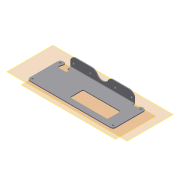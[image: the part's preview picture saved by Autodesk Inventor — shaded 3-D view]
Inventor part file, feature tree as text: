
AUTODESK INVENTOR PART (.ipt)
format: ipt  version: 2014 (Build 180170000, 170)  size: 222,720 bytes
history: native  units: mm
features: fillet x6, sketch x5, sheet_metal_op x4, reference x4, extrude x3, plane x2, other x2
ambient origin geometry x8: Origin, YZ Plane, XZ Plane, XY Plane, X Axis, Y Axis, Z Axis, Center Point
bodies: Solid1 (feature_tree)
feature tree (26):
  plane  "Work Plane1"
  sheet_metal_op  "Face1"
  fillet  "Fillet1"  Radius=1.0mm
  plane  "Work Plane2"
  extrude  "Extrusion4"  Depth=1.0mm
  sheet_metal_op  "Flange3"
  fillet  "Fillet2"  Radius=1.0mm
  fillet  "Fillet3"  Radius=5.0mm
  extrude  "Extrusion5"  Depth=5.0mm
  fillet  "Fillet4"  Radius=7.0mm
  fillet  "Fillet5"  Radius=1.5mm
  extrude  "Extrusion6"  Depth=5.0mm
  fillet  "Fillet6"  Radius=10.0mm
  sketch  "Sketch1"  dims[d1=1.0mm d2=1.0mm d3=1.0mm d4=5.0mm]
  reference  "Reference1"
  reference  "Reference2"
  reference  "Reference3"
  reference  "Reference4"
  other  "Plate1"
  sketch  "Sketch7"  dims[d5=7.0mm d6=5.0mm d7=7.0mm d8=1.5mm]
  sketch  "Sketch8"  dims[d48=1.0mm d49=5.0mm d50=10.0mm]
  other  "Plate4"
  sheet_metal_op  "Bend3"
  sheet_metal_op  "Corner3"
  sketch  "Sketch9"  dims[d51=10.0mm]
  sketch  "Sketch10"  dims[d52=10.0mm d53=5.0mm d54=0.1mm d55=2.0mm d56=0.0mm d57=1.5mm d58=0.75mm d59=3.0mm d60=1.5mm d61=20.0mm d62=16.057029mm d63=1.5mm d64=6.0mm d65=1.5mm d66=1.5mm d67=5.0mm d68=2.0mm d69=3.0mm d70=3.0mm d71=3.0mm d72=3.0mm d73=5.0mm d74=5.0mm d75=30.0mm d76=30.0mm d77=11.0mm d78=11.0mm d79=11.0mm d80=11.0mm d81=2.0mm d82=0.0mm d83=10.0mm d84=2.0mm d85=5.0mm d86=10.0mm d87=0.0mm d88=10.0mm]
